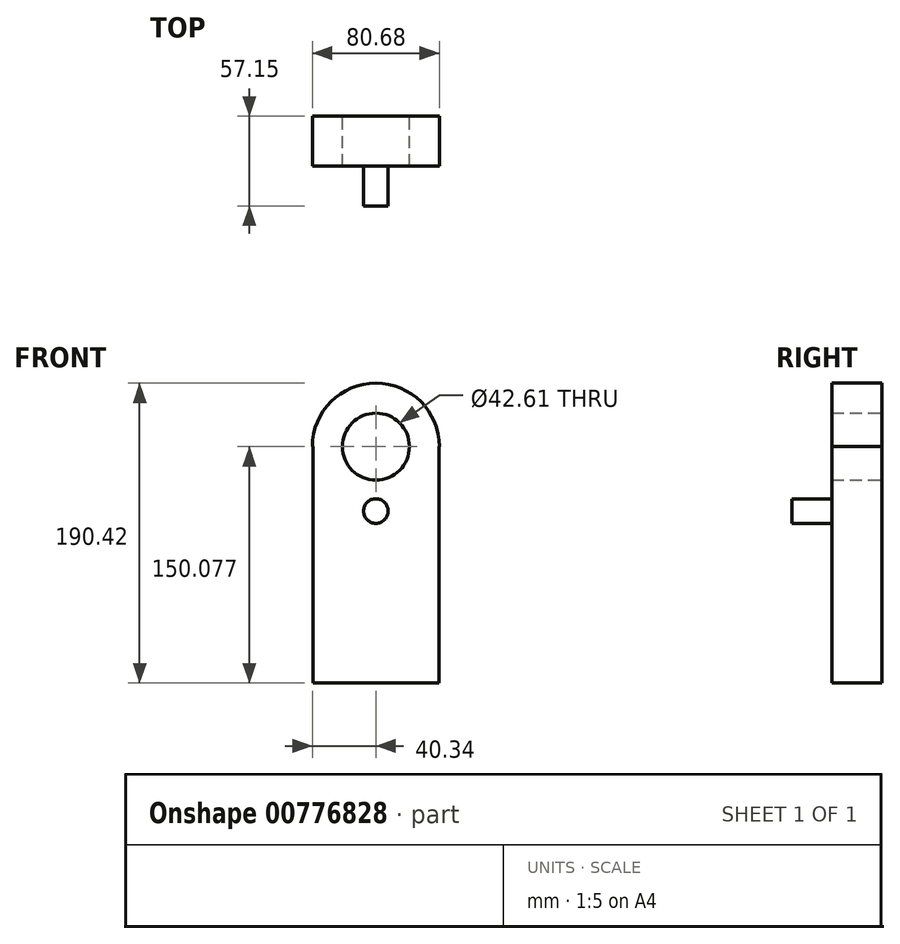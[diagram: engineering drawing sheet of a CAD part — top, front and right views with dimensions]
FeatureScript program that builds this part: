
annotation { "Feature Type Name" : "Feature", "Feature Type Description" : "" }
export const myFeature = defineFeature(function(context is Context, id is Id, definition is map)
    precondition{}
    {
        {
            var Q0;
            Q0=qCreatedBy(makeId("Front.planeOp"),FACE);
            var sketch = newSketch(context, id + "F0", { "sketchPlane" : qUnion([Q0])});
            skLineSegment(sketch, "E0.bottom", {"start": v(39.98, -75.04) * mm, "end": v(-39.98, -75.04) * mm});
            skLineSegment(sketch, "E0.top", {"start": v(40.34, 75.04) * mm, "end": v(39.98, 75.04) * mm});
            skLineSegment(sketch, "E0.left", {"start": v(39.98, -75.04) * mm, "end": v(39.98, 75.04) * mm});
            skLineSegment(sketch, "E0.right", {"start": v(-39.98, -75.04) * mm, "end": v(-39.98, 75.04) * mm});
            skPoint(sketch, "E0.middle", {"position": v(0, 0) * mm});
            skArc(sketch, "E1", {"start": v(40.34, 75.04) * mm, "mid": v(0, 115.38) * mm, "end": v(-40.34, 75.04) * mm});
            skLineSegment(sketch, "E2.trimOffspring", {"start": v(-39.98, 75.04) * mm, "end": v(-40.34, 75.04) * mm});
            skCircle(sketch, "E3", {"center": v(0, 75.04) * mm, "radius": 21.3 * mm});
            skSolve(sketch);
        }
        {
            var Q0;
            Q0 = qSketchRegion(id + "F0", true);
            extrude(context, id + "F1", {"entities" : qUnion([Q0]), "depth" : 31.75 * mm, "offsetDistance" : 25.4 * mm});
        }
        {
            var Q0;
            Q0=makeQuery(id+"F1.opExtrude","CAP_FACE",FACE,{"disambiguationData":[OSD([sQuery(id+"F0.wireOp",EDGE,"E0.bottom"),sQuery(id+"F0.wireOp",EDGE,"E0.top"),sQuery(id+"F0.wireOp",EDGE,"E0.left"),sQuery(id+"F0.wireOp",EDGE,"E0.right"),sQuery(id+"F0.wireOp",EDGE,"E1"),sQuery(id+"F0.wireOp",EDGE,"E2.trimOffspring"),sQuery(id+"F0.wireOp",EDGE,"E3")])],"isStart":false});
            var sketch = newSketch(context, id + "F2", { "sketchPlane" : qUnion([Q0])});
            skCircle(sketch, "E4", {"center": v(0, 34.13) * mm, "radius": 7.8 * mm});
            skSolve(sketch);
        }
        {
            var Q0;
            Q0 = qSketchRegion(id + "F2", true);
            extrude(context, id + "F3", {"entities" : qUnion([Q0]), "operationType" : NewBodyOperationType.ADD, "depth" : 25.4 * mm, "offsetDistance" : 25.4 * mm});
        }
    });
